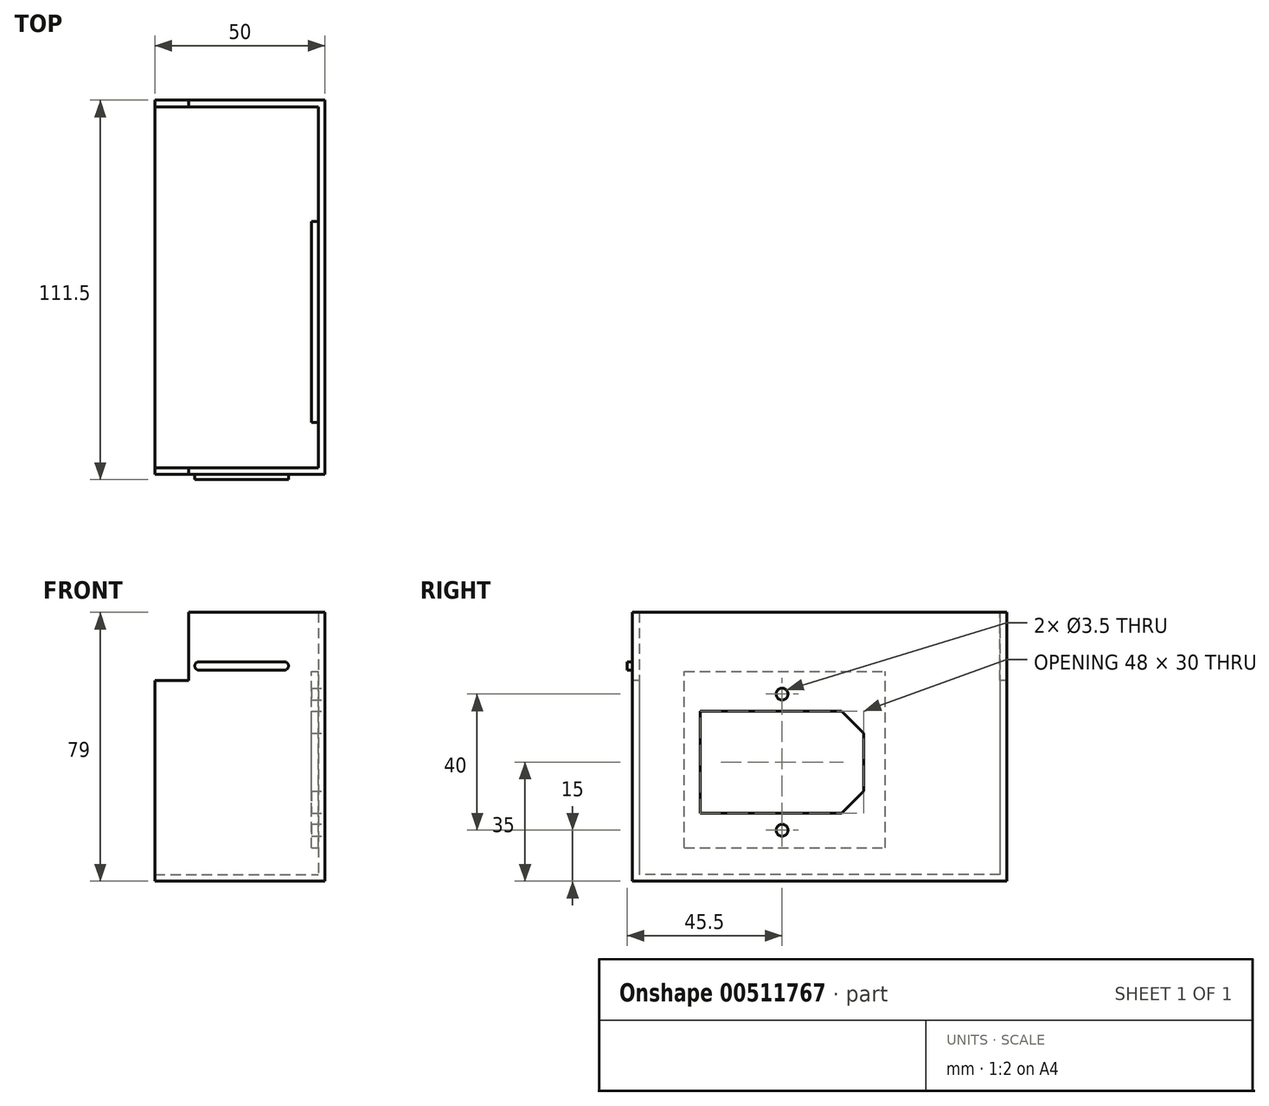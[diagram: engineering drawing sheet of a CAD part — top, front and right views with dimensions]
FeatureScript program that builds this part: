
annotation { "Feature Type Name" : "Feature", "Feature Type Description" : "" }
export const myFeature = defineFeature(function(context is Context, id is Id, definition is map)
    precondition{}
    {
        {
            var Q0;
            Q0=qCreatedBy(makeId("Top.planeOp"),FACE);
            var sketch = newSketch(context, id + "F0", { "sketchPlane" : qUnion([Q0])});
            skLineSegment(sketch, "E0", {"start": v(-50, 110) * mm, "end": v(0, 110) * mm});
            skLineSegment(sketch, "E1", {"start": v(0, 110) * mm, "end": v(0, 0) * mm});
            skLineSegment(sketch, "E2", {"start": v(0, 0) * mm, "end": v(-50, 0) * mm});
            skLineSegment(sketch, "E3.0", {"start": v(-2, 2) * mm, "end": v(-50, 2) * mm});
            skLineSegment(sketch, "E3.1", {"start": v(-2, 108) * mm, "end": v(-2, 2) * mm});
            skLineSegment(sketch, "E3.2", {"start": v(-50, 108) * mm, "end": v(-2, 108) * mm});
            skLineSegment(sketch, "E4", {"start": v(-50, 110) * mm, "end": v(-50, 108) * mm});
            skLineSegment(sketch, "E5", {"start": v(-50, 2) * mm, "end": v(-50, 0) * mm});
            skSolve(sketch);
        }
        {
            var Q0;
            Q0 = qSketchRegion(id + "F0", true);
            extrude(context, id + "F1", {"entities" : qUnion([Q0]), "depth" : 79 * mm});
        }
        {
            var Q0;
            Q0=makeQuery(id+"F1.opExtrude","SWEPT_FACE",FACE,{"disambiguationData":[OSD([sQuery(id+"F0.wireOp",EDGE,"E3.1")])]});
            var sketch = newSketch(context, id + "F2", { "sketchPlane" : qUnion([Q0])});
            skLineSegment(sketch, "E6.bottom", {"start": v(-108, 0) * mm, "end": v(-2, 0) * mm});
            skLineSegment(sketch, "E6.top", {"start": v(-108, 2) * mm, "end": v(-2, 2) * mm});
            skLineSegment(sketch, "E6.left", {"start": v(-108, 0) * mm, "end": v(-108, 2) * mm});
            skLineSegment(sketch, "E6.right", {"start": v(-2, 0) * mm, "end": v(-2, 2) * mm});
            skSolve(sketch);
        }
        {
            var Q0;
            Q0 = qSketchRegion(id + "F2", true);
            extrude(context, id + "F3", {"entities" : qUnion([Q0]), "operationType" : NewBodyOperationType.ADD, "depth" : 48 * mm});
        }
        {
            var Q0;
            Q0=makeQuery(id+"F1.opExtrude","SWEPT_FACE",FACE,{"disambiguationData":[OSD([sQuery(id+"F0.wireOp",EDGE,"E2")])]});
            var sketch = newSketch(context, id + "F4", { "sketchPlane" : qUnion([Q0])});
            skLineSegment(sketch, "E7.bottom", {"start": v(-50, 79) * mm, "end": v(-40, 79) * mm});
            skLineSegment(sketch, "E7.top", {"start": v(-50, 59) * mm, "end": v(-40, 59) * mm});
            skLineSegment(sketch, "E7.left", {"start": v(-50, 79) * mm, "end": v(-50, 59) * mm});
            skLineSegment(sketch, "E7.right", {"start": v(-40, 79) * mm, "end": v(-40, 59) * mm});
            skSolve(sketch);
        }
        {
            var Q0;
            Q0 = qSketchRegion(id + "F4", true);
            extrude(context, id + "F5", {"entities" : qUnion([Q0]), "operationType" : NewBodyOperationType.REMOVE, "oppositeDirection" : true, "depth" : 150 * mm});
        }
        {
            var Q0;
            Q0=makeQuery(id+"F1.opExtrude","SWEPT_FACE",FACE,{"disambiguationData":[OSD([sQuery(id+"F0.wireOp",EDGE,"E3.1")])]});
            var sketch = newSketch(context, id + "F6", { "sketchPlane" : qUnion([Q0])});
            skLineSegment(sketch, "E8.bottom", {"start": v(-15.28, 9.81) * mm, "end": v(-74.37, 9.81) * mm});
            skLineSegment(sketch, "E8.top", {"start": v(-15.28, 61.68) * mm, "end": v(-74.37, 61.68) * mm});
            skLineSegment(sketch, "E8.left", {"start": v(-15.28, 9.81) * mm, "end": v(-15.28, 61.68) * mm});
            skLineSegment(sketch, "E8.right", {"start": v(-74.37, 9.81) * mm, "end": v(-74.37, 61.68) * mm});
            skSolve(sketch);
        }
        {
            var Q0;
            Q0 = qSketchRegion(id + "F6", true);
            extrude(context, id + "F7", {"entities" : qUnion([Q0]), "operationType" : NewBodyOperationType.ADD, "depth" : 2 * mm});
        }
        {
            var Q0;
            Q0=makeQuery(id+"F1.opExtrude","SWEPT_FACE",FACE,{"disambiguationData":[OSD([sQuery(id+"F0.wireOp",EDGE,"E1")])]});
            var sketch = newSketch(context, id + "F8", { "sketchPlane" : qUnion([Q0])});
            skLineSegment(sketch, "E9.bottom", {"start": v(20, 50) * mm, "end": v(61.5, 50) * mm});
            skLineSegment(sketch, "E9.top", {"start": v(20, 20) * mm, "end": v(61.5, 20) * mm});
            skLineSegment(sketch, "E9.left", {"start": v(20, 50) * mm, "end": v(20, 20) * mm});
            skLineSegment(sketch, "E9.right", {"start": v(68, 43.5) * mm, "end": v(68, 26.5) * mm});
            skLineSegment(sketch, "E10", {"start": v(44, 79) * mm, "end": v(44, -6.7) * mm, "construction": true});
            skPoint(sketch, "E10.startSnap0", {"position": v(44, 50) * mm});
            skPoint(sketch, "E10.endSnap0", {"position": v(44, 20) * mm});
            skLineSegment(sketch, "E11", {"start": v(7.58, 35) * mm, "end": v(83.82, 35) * mm, "construction": true});
            skPoint(sketch, "E11.startSnap0", {"position": v(20, 35) * mm});
            skCircle(sketch, "E12", {"center": v(44, 55) * mm, "radius": 1.75 * mm});
            skCircle(sketch, "E13.MirrorC", {"center": v(44, 15) * mm, "radius": 1.75 * mm});
            skLineSegment(sketch, "E14", {"start": v(61.5, 50) * mm, "end": v(68, 43.5) * mm});
            skLineSegment(sketch, "E15.MirrorCS", {"start": v(61.5, 20) * mm, "end": v(68, 26.5) * mm});
            skPoint(sketch, "E16.orphan", {"position": v(68, 50) * mm});
            skPoint(sketch, "E17.orphan", {"position": v(68, 20) * mm});
            skSolve(sketch);
        }
        {
            var Q0;
            Q0 = qSketchRegion(id + "F8", true);
            extrude(context, id + "F9", {"entities" : qUnion([Q0]), "operationType" : NewBodyOperationType.REMOVE, "oppositeDirection" : true, "depth" : 25 * mm});
        }
        {
            var Q0;
            Q0=makeQuery(id+"F1.opExtrude","SWEPT_FACE",FACE,{"disambiguationData":[OSD([sQuery(id+"F0.wireOp",EDGE,"E2")])]});
            var sketch = newSketch(context, id + "F10", { "sketchPlane" : qUnion([Q0])});
            skArc(sketch, "E18", {"start": v(-12, 62) * mm, "mid": v(-10.75, 63.25) * mm, "end": v(-12, 64.5) * mm});
            skArc(sketch, "E19", {"start": v(-37, 64.5) * mm, "mid": v(-38.25, 63.25) * mm, "end": v(-37, 62) * mm});
            skLineSegment(sketch, "E20", {"start": v(-37, 64.5) * mm, "end": v(-12, 64.5) * mm});
            skLineSegment(sketch, "E21", {"start": v(-37, 62) * mm, "end": v(-12, 62) * mm});
            skLineSegment(sketch, "E22.0", {"start": v(-50, 59) * mm, "end": v(-40, 59) * mm});
            skSolve(sketch);
        }
        {
            var Q0;
            Q0 = qSketchRegion(id + "F10", true);
            extrude(context, id + "F11", {"entities" : qUnion([Q0]), "operationType" : NewBodyOperationType.ADD, "depth" : 1.5 * mm});
        }
    });
